# Revit family: LM0146831_Mueble Plus 120 cm con Lavamanos Cascade Derecho
name_source: partatom
category: Furniture
units: mm (PartAtom-declared; Revit-internal decimal feet)

## family parameters
Always vertical = Yes
Cut with Voids When Loaded = No
OmniClass Number = 23.31.25.13
OmniClass Title = Bathroom Cabinets
Room Calculation Point = No
Shared = No
Work Plane-Based = No

## types (1)
- LM0146831_Mueble Plus 120 cm con Lavamanos Cascade Derecho
    Alto = 425 mm  [stored 1.39436 ft]
    Ancho = 1196 mm  [stored 3.92388 ft]
    Canto = PVC rígido 22 mm de calibre.
    Creado por = BIMABU
    Default Elevation = 0 mm  [stored 0 ft]
    Densidad = 25mm 597 kg./m^3.
    Dimensiones generales del producto = 16,73” x 47,09” x 19,69” (425 x 1196 x 500 mm).
    Fecha de creación = 16/03/2021
    Manufacturer = Corona
    Material = Corona_Porcelana_Sanitaria
    Material 2 = Corona_Madera_Aglomerada_Duna
    Material 3 = Corona_Madera_Onix
    Model = Mueble Plus 120cm
    Peso Bruto aprox = 82,5 lb (37,4 kg).
    Peso Neto aprox = 71,2 lb (32,3 kg).
    Profundidad = 500 mm  [stored 1.64042 ft]
    Resistencia a la humedad = 8%.
    Resistencia al rayado = 700 ciclos.
    URL = https://corona.co

note: [stored X ft] marks values corroborated as IEEE doubles in the binary element streams (Revit-internal decimal feet)

## geometry (parser evidence)
native form markers: Sweep x6
no freeform markers — native parametric forms only
